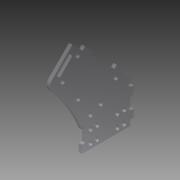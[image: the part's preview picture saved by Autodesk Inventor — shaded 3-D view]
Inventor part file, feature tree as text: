
AUTODESK INVENTOR PART (.ipt)
format: ipt  version: 2015 (Build 190159000, 159)  size: 332,800 bytes
history: native  units: mm
features: extrude x9, sketch x9, projected_geometry x5, fillet x1
ambient origin geometry x8: Origin, YZ Plane, XZ Plane, XY Plane, X Axis, Y Axis, Z Axis, Center Point
bodies: Solid1 (feature_tree)
feature tree (24):
  extrude  "Extrusion1"  TaperAngle=135.0deg  [1 undecoded]
  extrude  "Extrusion2"  Depth=3.0mm
  extrude  "Extrusion3"  Depth=10.0mm
  extrude  "Extrusion4"  Depth=10.0mm
  extrude  "Extrusion5"  Depth=5.0mm
  extrude  "Extrusion6"  Depth=7.0mm
  extrude  "Extrusion7"  Depth=3.0mm TaperAngle=0.0deg
  extrude  "Extrusion8"  Depth=6.0mm
  extrude  "Extrusion9"  Depth=3.0mm
  fillet  "Fillet2"  Radius=13.0mm
  sketch  "Sketch1"  dims[d3=40.0mm d5=135.0deg]
  sketch  "Sketch2"  dims[d6=28.0mm d8=3.0mm d10=73.0mm]
  sketch  "Sketch3"  dims[d11=37.0mm d14=10.0mm]
  projected_geometry  "Projected Loop1"
  sketch  "Sketch4"  dims[d15=10.0mm d16=10.0mm]
  projected_geometry  "Projected Loop2"
  sketch  "Sketch5"  dims[d17=7.0mm d18=5.0mm]
  projected_geometry  "Projected Loop3"
  sketch  "Sketch6"  dims[d19=7.0mm d20=7.0mm]
  sketch  "Sketch8"  dims[d21=3.0mm d23=3.0mm d24=0.0mm]
  sketch  "Sketch9"  dims[d25=6.0mm d26=6.0mm]
  projected_geometry  "Projected Loop5"
  sketch  "Sketch10"  dims[d27=3.0mm d28=3.0mm d29=13.0mm d30=3.0mm d31=3.0mm d32=6.0mm d33=4.5mm d34=19.0mm d35=3.0mm d36=3.0mm d37=3.0mm d38=48.0mm d39=3.0mm d40=0.0mm d41=3.0mm d42=0.0mm d44=3.0mm d45=3.0mm d46=0.0mm d47=3.0mm d48=7.0mm d49=3.0mm d50=0.0mm d51=3.0mm d52=3.0mm d53=3.0mm d54=3.0mm d55=3.0mm d56=3.0mm d57=3.0mm d58=3.0mm d59=3.0mm d60=3.0mm d61=0.0mm d62=3.599mm d63=5.0mm d64=11.0mm d65=6.0mm d66=6.0mm d67=5.0mm d68=11.0mm d70=4.0mm d71=3.0mm d72=0.0mm d73=3.0mm d74=0.0mm d75=28.0mm d76=3.0mm d77=36.0mm d78=3.0mm d79=0.0mm d80=6.0mm]
  projected_geometry  "Projected Loop6"
note: 1 required parameter value undecoded (feature->parameter linkage not recoverable at this tier; creation-order binding heuristic only, values carry confidence <= 0.55)
